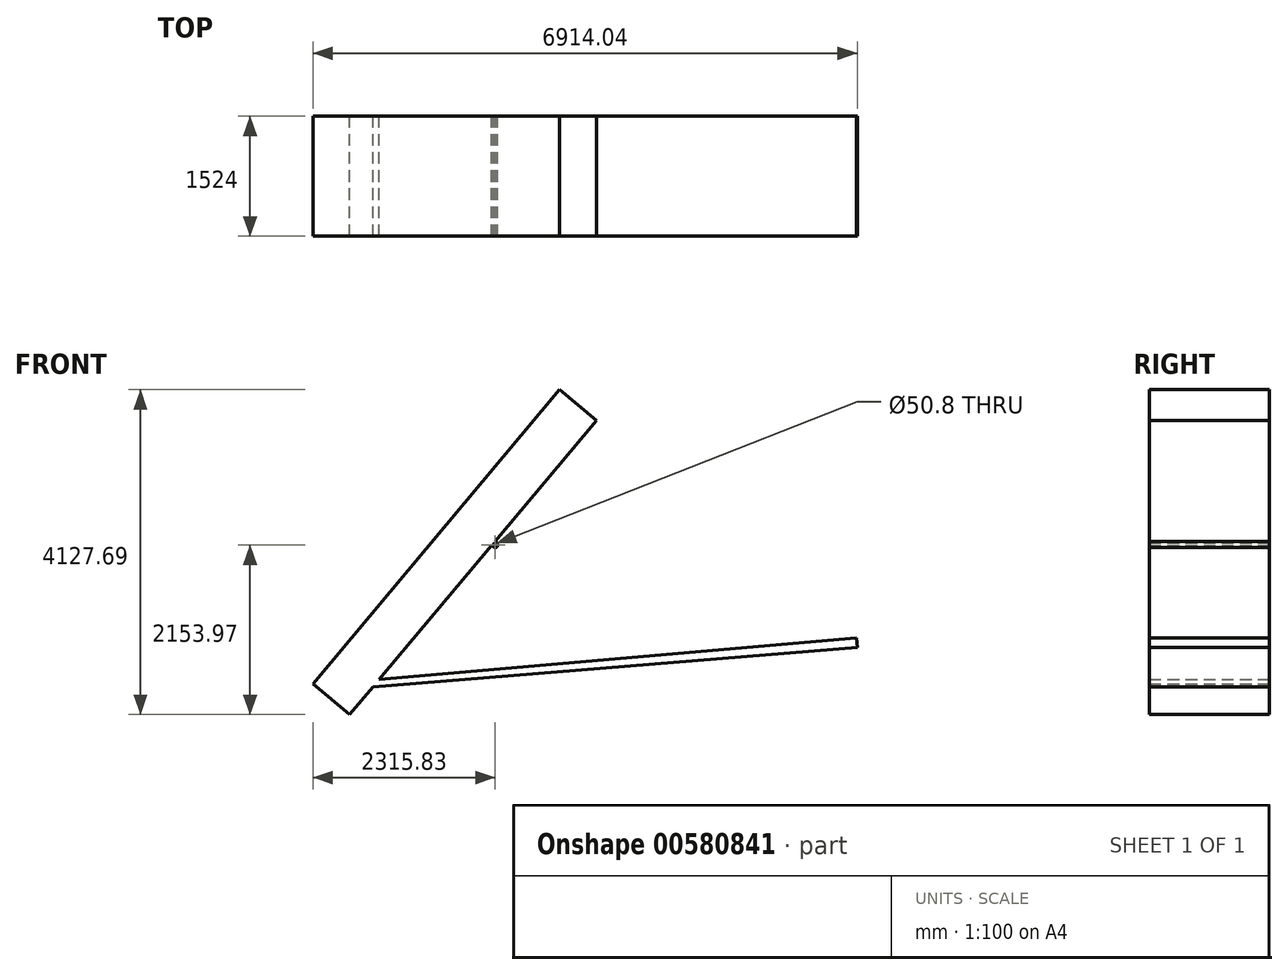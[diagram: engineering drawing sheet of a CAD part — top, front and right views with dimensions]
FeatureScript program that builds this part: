
annotation { "Feature Type Name" : "Feature", "Feature Type Description" : "" }
export const myFeature = defineFeature(function(context is Context, id is Id, definition is map)
    precondition{}
    {
        {
            var Q0;
            Q0=qCreatedBy(makeId("Front.planeOp"),FACE);
            var sketch = newSketch(context, id + "F0", { "sketchPlane" : qUnion([Q0])});
            skLineSegment(sketch, "E0", {"start": v(-838.46, 1581.88) * mm, "end": v(-2128.28, 44.73) * mm});
            skLineSegment(sketch, "E1", {"start": v(-3973.2, -2153.97) * mm, "end": v(-4440.19, -1762.13) * mm});
            skLineSegment(sketch, "E2", {"start": v(-838.46, 1581.88) * mm, "end": v(-1305.44, 1973.72) * mm});
            skLineSegment(sketch, "E3", {"start": v(-1305.44, 1973.72) * mm, "end": v(-4440.19, -1762.13) * mm});
            skLineSegment(sketch, "E4.right", {"start": v(2473.85, -1302.74) * mm, "end": v(2462.78, -1176.22) * mm});
            skCircle(sketch, "E5", {"center": v(-2124.36, 0) * mm, "radius": 25.4 * mm});
            skArc(sketch, "E6", {"start": v(-2144.77, -24.32) * mm, "mid": v(-2100.04, -20.4) * mm, "end": v(-2103.96, 24.32) * mm});
            skLineSegment(sketch, "E7", {"start": v(-2169.1, -3.91) * mm, "end": v(-2144.77, -24.32) * mm});
            skLineSegment(sketch, "E8", {"start": v(-2103.96, 24.32) * mm, "end": v(-2128.28, 44.73) * mm});
            skLineSegment(sketch, "E9.trimOffspring", {"start": v(-2169.1, -3.91) * mm, "end": v(-3597.69, -1706.45) * mm});
            skLineSegment(sketch, "E10.trimOffspring", {"start": v(-3679.32, -1803.73) * mm, "end": v(-3973.2, -2153.97) * mm});
            skLineSegment(sketch, "E11", {"start": v(-3597.69, -1706.45) * mm, "end": v(2462.78, -1176.22) * mm});
            skLineSegment(sketch, "E12", {"start": v(-3679.32, -1803.73) * mm, "end": v(2473.85, -1302.74) * mm});
            skSolve(sketch);
        }
        {
            var Q0;
            {var subQ1=sQuery(id+"F0.wireOp",EDGE,"E1");Q0=makeQuery(id+"F0.imprint","IMPRINT",FACE,{"disambiguationData":[TD([[makeQuery(id+"F0.imprint","IMPRINT",EDGE,{"derivedFrom":subQ1}),-1.0]])]});}
            var Q1;
            Q1=makeQuery(id+"F0.imprint","IMPRINT",FACE,{"disambiguationData":[TD([[makeQuery(id+"F0.imprint","IMPRINT",EDGE,{"derivedFrom":sQuery(id+"F0.wireOp",EDGE,"E4.bottom")}),-1.0]])]});
            extrude(context, id + "F1", {"entities" : qUnion([Q0, Q1]), "depth" : 1524 * mm, "offsetDistance" : 25.4 * mm});
        }
    });
